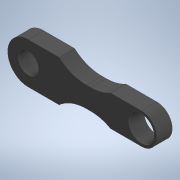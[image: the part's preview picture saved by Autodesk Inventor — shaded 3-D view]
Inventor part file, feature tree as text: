
AUTODESK INVENTOR PART (.ipt)
format: ipt  version: 2022 (Build 260153000, 153)  size: 148,480 bytes
history: native  units: mm
features: fillet x2, extrude x1, sketch x1
ambient origin geometry x8: Origin, YZ Plane, XZ Plane, XY Plane, X Axis, Y Axis, Z Axis, Center Point
bodies: Solid1 (feature_tree)
feature tree (4):
  extrude  "Extrusion1"  Depth=4.0mm
  fillet  "Fillet1"  Radius=6.0mm
  fillet  "Fillet2"  Radius=5.0mm
  sketch  "Sketch1"  dims[d0=8.0mm d1=4.0mm d8=6.0mm d9=5.0mm d10=6.0mm d11=6.0mm d12=6.0mm d13=3.0mm d14=0.0mm d15=8.0mm d16=8.0mm d17=10.0mm d19=4.0mm]
